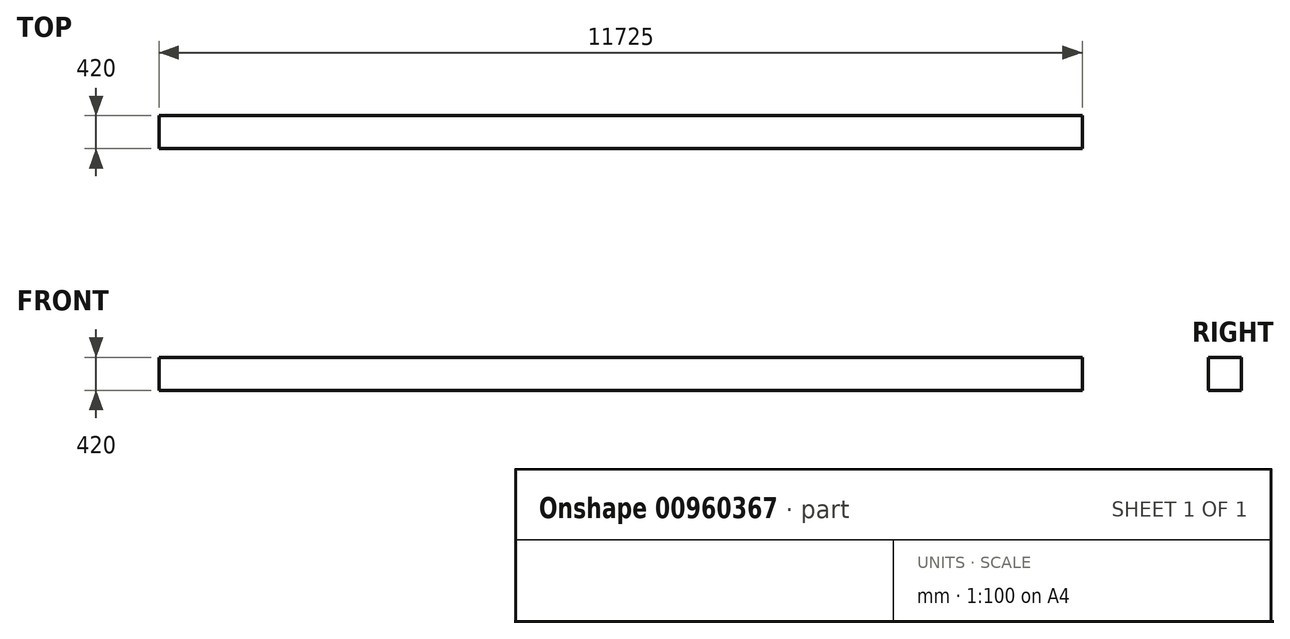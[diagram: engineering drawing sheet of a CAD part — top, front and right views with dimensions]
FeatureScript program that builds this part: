
annotation { "Feature Type Name" : "Feature", "Feature Type Description" : "" }
export const myFeature = defineFeature(function(context is Context, id is Id, definition is map)
    precondition{}
    {
        {
            var Q0;
            Q0=qCreatedBy(makeId("Right.planeOp"),FACE);
            var sketch = newSketch(context, id + "F0", { "sketchPlane" : qUnion([Q0])});
            skLineSegment(sketch, "E0", {"start": v(254.88, 438.78) * mm, "end": v(254.88, 18.78) * mm});
            skLineSegment(sketch, "E1", {"start": v(254.88, 18.78) * mm, "end": v(-165.12, 18.78) * mm});
            skLineSegment(sketch, "E2", {"start": v(-165.12, 18.78) * mm, "end": v(-165.12, 438.78) * mm});
            skLineSegment(sketch, "E3", {"start": v(-165.12, 438.78) * mm, "end": v(254.88, 438.78) * mm});
            skSolve(sketch);
        }
        {
            var Q0;
            Q0=makeQuery(id+"F0.imprint","IMPRINT",FACE,{"disambiguationData":[TD([[makeQuery(id+"F0.imprint","IMPRINT",EDGE,{"derivedFrom":sQuery(id+"F0.wireOp",EDGE,"E0")}),-1.0]])]});
            extrude(context, id + "F1", {"entities" : qUnion([Q0]), "depth" : 11725 * mm, "offsetDistance" : 25 * mm});
        }
    });
